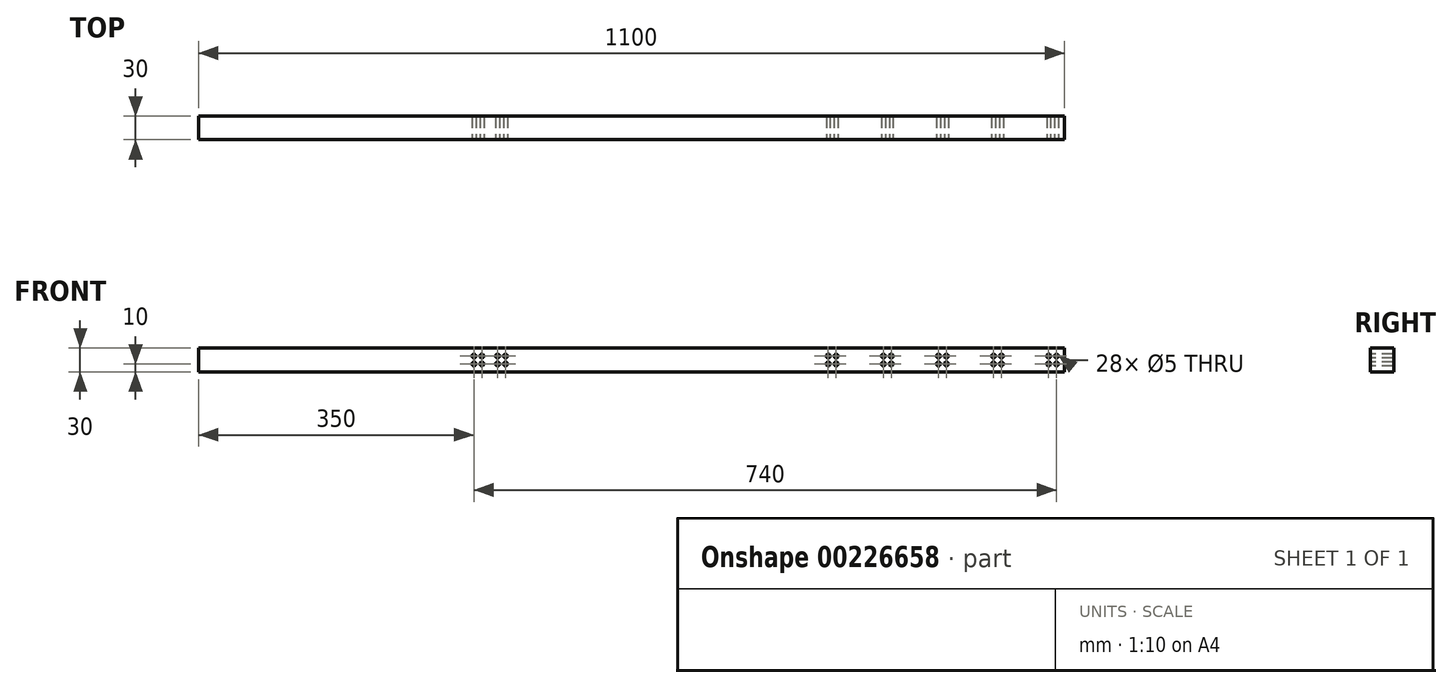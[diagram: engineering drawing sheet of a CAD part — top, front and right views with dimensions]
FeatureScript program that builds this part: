
annotation { "Feature Type Name" : "Feature", "Feature Type Description" : "" }
export const myFeature = defineFeature(function(context is Context, id is Id, definition is map)
    precondition{}
    {
        {
            var Q0;
            Q0=qCreatedBy(makeId("Front.planeOp"),FACE);
            var sketch = newSketch(context, id + "F0", { "sketchPlane" : qUnion([Q0])});
            skLineSegment(sketch, "E0.bottom", {"start": v(-550, 15) * mm, "end": v(550, 15) * mm});
            skLineSegment(sketch, "E0.top", {"start": v(-550, -15) * mm, "end": v(550, -15) * mm});
            skLineSegment(sketch, "E0.left", {"start": v(-550, 15) * mm, "end": v(-550, -15) * mm});
            skLineSegment(sketch, "E0.right", {"start": v(550, 15) * mm, "end": v(550, -15) * mm});
            skLineSegment(sketch, "E1", {"start": v(0, 15) * mm, "end": v(0, -15) * mm, "construction": true});
            skLineSegment(sketch, "E2", {"start": v(-550, 0) * mm, "end": v(550, 0) * mm, "construction": true});
            skSolve(sketch);
        }
        {
            var Q0;
            Q0=makeQuery(id+"F0.imprint","IMPRINT",FACE,{"disambiguationData":[TD([[makeQuery(id+"F0.imprint","IMPRINT",EDGE,{"derivedFrom":sQuery(id+"F0.wireOp",EDGE,"E0.bottom")}),-1.0]])]});
            extrude(context, id + "F1", {"entities" : qUnion([Q0]), "endBound" : BoundingType.SYMMETRIC, "depth" : 30 * mm});
        }
        {
            var Q0;
            Q0=makeQuery(id+"F1.opExtrude","CAP_FACE",FACE,{"disambiguationData":[OSD([sQuery(id+"F0.wireOp",EDGE,"E0.bottom"),sQuery(id+"F0.wireOp",EDGE,"E0.top"),sQuery(id+"F0.wireOp",EDGE,"E0.left"),sQuery(id+"F0.wireOp",EDGE,"E0.right")])],"isStart":false});
            var sketch = newSketch(context, id + "F2", { "sketchPlane" : qUnion([Q0])});
            skPoint(sketch, "E3", {"position": v(-170, 5) * mm});
            skPoint(sketch, "E4", {"position": v(-160, 5) * mm});
            skPoint(sketch, "E5", {"position": v(-170, -5) * mm});
            skPoint(sketch, "E6", {"position": v(-160, -5) * mm});
            skPoint(sketch, "E7", {"position": v(530, 5) * mm});
            skPoint(sketch, "E8", {"position": v(540, 5) * mm});
            skPoint(sketch, "E9", {"position": v(540, -5) * mm});
            skPoint(sketch, "E10", {"position": v(530, -5) * mm});
            skPoint(sketch, "E11", {"position": v(470, 5) * mm});
            skPoint(sketch, "E12", {"position": v(470, -5) * mm});
            skPoint(sketch, "E13", {"position": v(460, 5) * mm});
            skPoint(sketch, "E14", {"position": v(460, -5) * mm});
            skPoint(sketch, "E15", {"position": v(400, 5) * mm});
            skPoint(sketch, "E16", {"position": v(400, -5) * mm});
            skPoint(sketch, "E17", {"position": v(390, 5) * mm});
            skPoint(sketch, "E18", {"position": v(390, -5) * mm});
            skPoint(sketch, "E19", {"position": v(330, 5) * mm});
            skPoint(sketch, "E20", {"position": v(330, -5) * mm});
            skPoint(sketch, "E21", {"position": v(320, 5) * mm});
            skPoint(sketch, "E22", {"position": v(320, -5) * mm});
            skPoint(sketch, "E23", {"position": v(260, 5) * mm});
            skPoint(sketch, "E24", {"position": v(260, -5) * mm});
            skPoint(sketch, "E25", {"position": v(250, 5) * mm});
            skPoint(sketch, "E26", {"position": v(250, -5) * mm});
            skPoint(sketch, "E27", {"position": v(-190, 5) * mm});
            skPoint(sketch, "E28", {"position": v(-190, -5) * mm});
            skPoint(sketch, "E29", {"position": v(-200, 5) * mm});
            skPoint(sketch, "E30", {"position": v(-200, -5) * mm});
            skSolve(sketch);
        }
        {
            var Q0;
            Q0=sQuery(id+"F2.wireOp",VERTEX,"E3");
            var Q1;
            Q1=sQuery(id+"F2.wireOp",VERTEX,"E5");
            var Q2;
            Q2=sQuery(id+"F2.wireOp",VERTEX,"E6");
            var Q3;
            Q3=sQuery(id+"F2.wireOp",VERTEX,"E4");
            var Q4;
            Q4=sQuery(id+"F2.wireOp",VERTEX,"E7");
            var Q5;
            Q5=sQuery(id+"F2.wireOp",VERTEX,"E10");
            var Q6;
            Q6=sQuery(id+"F2.wireOp",VERTEX,"E8");
            var Q7;
            Q7=sQuery(id+"F2.wireOp",VERTEX,"E9");
            var Q8;
            Q8=sQuery(id+"F2.wireOp",VERTEX,"E11");
            var Q9;
            Q9=sQuery(id+"F2.wireOp",VERTEX,"E13");
            var Q10;
            Q10=sQuery(id+"F2.wireOp",VERTEX,"E14");
            var Q11;
            Q11=sQuery(id+"F2.wireOp",VERTEX,"E12");
            var Q12;
            Q12=sQuery(id+"F2.wireOp",VERTEX,"E25");
            var Q13;
            Q13=sQuery(id+"F2.wireOp",VERTEX,"E26");
            var Q14;
            Q14=sQuery(id+"F2.wireOp",VERTEX,"E24");
            var Q15;
            Q15=sQuery(id+"F2.wireOp",VERTEX,"E23");
            var Q16;
            Q16=sQuery(id+"F2.wireOp",VERTEX,"E21");
            var Q17;
            Q17=sQuery(id+"F2.wireOp",VERTEX,"E22");
            var Q18;
            Q18=sQuery(id+"F2.wireOp",VERTEX,"E20");
            var Q19;
            Q19=sQuery(id+"F2.wireOp",VERTEX,"E19");
            var Q20;
            Q20=sQuery(id+"F2.wireOp",VERTEX,"E17");
            var Q21;
            Q21=sQuery(id+"F2.wireOp",VERTEX,"E18");
            var Q22;
            Q22=sQuery(id+"F2.wireOp",VERTEX,"E16");
            var Q23;
            Q23=sQuery(id+"F2.wireOp",VERTEX,"E15");
            var Q24;
            Q24=sQuery(id+"F2.wireOp",VERTEX,"E27");
            var Q25;
            Q25=sQuery(id+"F2.wireOp",VERTEX,"E29");
            var Q26;
            Q26=sQuery(id+"F2.wireOp",VERTEX,"E30");
            var Q27;
            Q27=sQuery(id+"F2.wireOp",VERTEX,"E28");
            var Q28;
            Q28=makeQuery(id+"F1.opExtrude","SWEPT_BODY",BODY,{"disambiguationData":[OSD([sQuery(id+"F0.wireOp",EDGE,"E0.bottom"),sQuery(id+"F0.wireOp",EDGE,"E0.top"),sQuery(id+"F0.wireOp",EDGE,"E0.left"),sQuery(id+"F0.wireOp",EDGE,"E0.right")])]});
            hole(context, id + "F3", {"style" : HoleStyle.SIMPLE, "endStyle" : HoleEndStyle.THROUGH, "holeDiameter" : 5 * mm, "locations" : qUnion([Q0, Q1, Q2, Q3, Q4, Q5, Q6, Q7, Q8, Q9, Q10, Q11, Q12, Q13, Q14, Q15, Q16, Q17, Q18, Q19, Q20, Q21, Q22, Q23, Q24, Q25, Q26, Q27]), "scope" : qUnion([Q28]), "isTappedThrough" : true});
        }
    });
